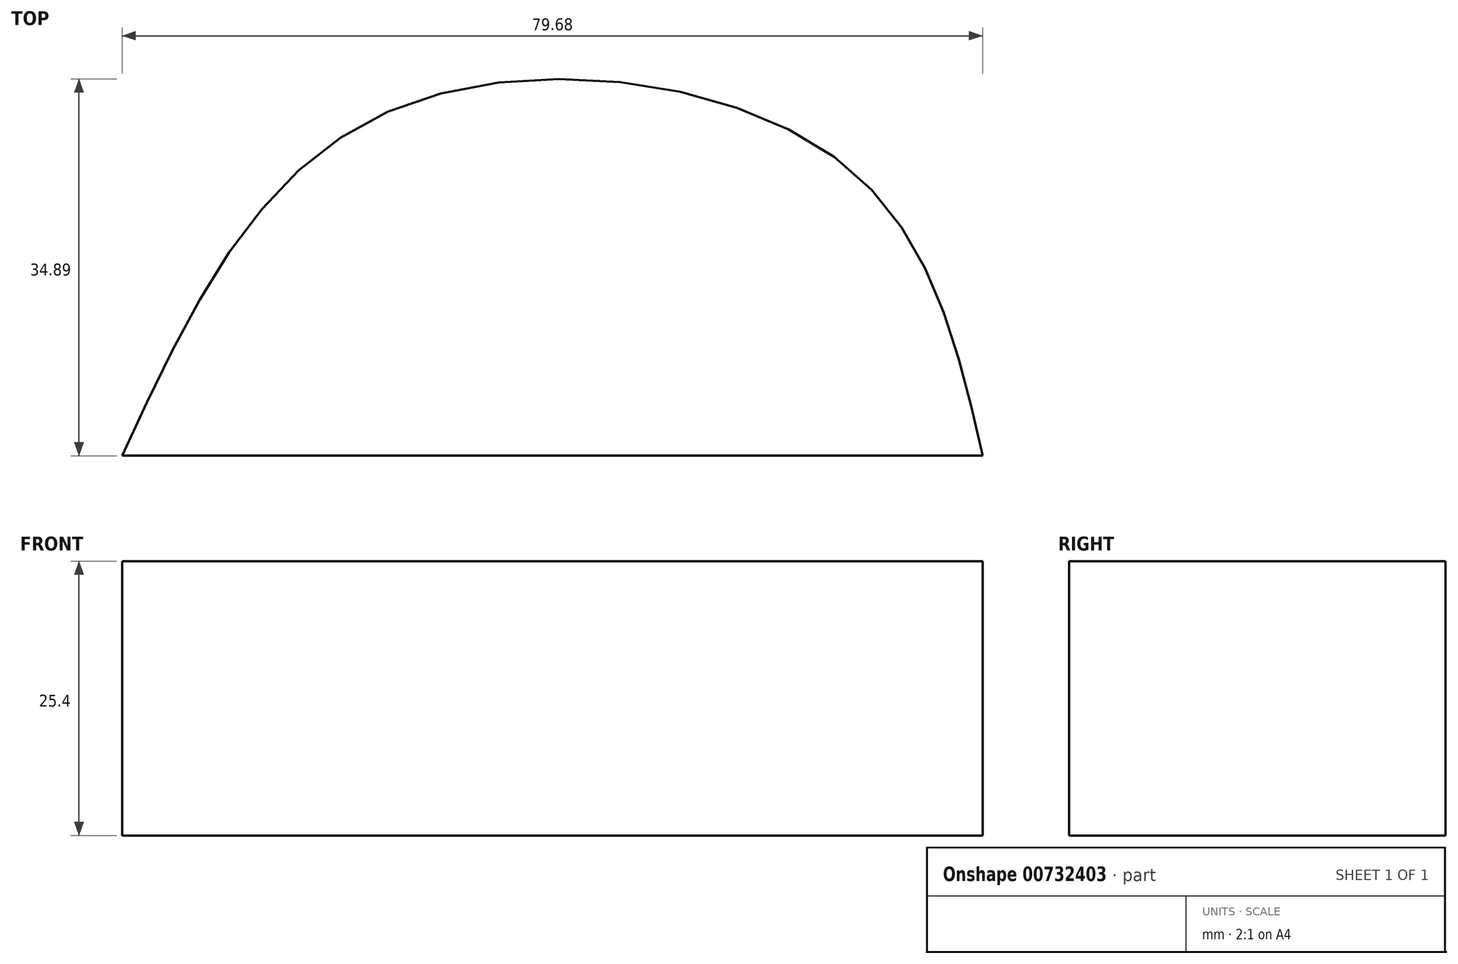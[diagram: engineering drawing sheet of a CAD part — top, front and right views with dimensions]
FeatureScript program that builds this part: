
annotation { "Feature Type Name" : "Feature", "Feature Type Description" : "" }
export const myFeature = defineFeature(function(context is Context, id is Id, definition is map)
    precondition{}
    {
        {
            var Q0;
            Q0=qCreatedBy(makeId("Top.planeOp"),FACE);
            var sketch = newSketch(context, id + "F0", { "sketchPlane" : qUnion([Q0])});
            skLineSegment(sketch, "E0", {"start": v(-113.46, 49.16) * mm, "end": v(-113.46, -27.26) * mm});
            skLineSegment(sketch, "E1", {"start": v(-113.46, -27.26) * mm, "end": v(100.4, -27.26) * mm});
            skLineSegment(sketch, "E2", {"start": v(100.4, -27.26) * mm, "end": v(100.4, 49.16) * mm});
            skLineSegment(sketch, "E3.top", {"start": v(-113.46, 75.25) * mm, "end": v(-7.22, 75.25) * mm});
            skLineSegment(sketch, "E3.left", {"start": v(-113.46, 49.16) * mm, "end": v(-113.46, 75.25) * mm});
            skLineSegment(sketch, "E3.right", {"start": v(-7.22, 49.16) * mm, "end": v(-7.22, 75.25) * mm});
            skCircle(sketch, "E4", {"center": v(100.4, -27.26) * mm, "radius": 20.7 * mm});
            skArc(sketch, "E5", {"start": v(122.3, 6.3) * mm, "mid": v(119.2, 31.73) * mm, "end": v(100.4, 49.16) * mm});
            skFitSpline(sketch, "E6", {"points": [v(122.3, 6.3) * mm, v(129.76, -16.07) * mm, v(119.74, -34.66) * mm], "startDerivative": vector(23.53, -44.9) * mm, "endDerivative": vector(-29.12, -36.95) * mm});
            skFitSpline(sketch, "E7", {"points": [v(-113.46, -27.26) * mm, v(-89.23, -58.94) * mm, v(-47.3, -54.75) * mm, v(-33.78, -27.26) * mm], "startDerivative": vector(52.37, -113.84) * mm, "endDerivative": vector(23.56, 104.18) * mm});
            skLineSegment(sketch, "E8", {"start": v(-7.22, 49.16) * mm, "end": v(100.4, 49.16) * mm});
            skFitSpline(sketch, "E9.MirrorCS", {"points": [v(-113.46, -27.26) * mm, v(-89.23, 4.43) * mm, v(-47.3, 0.23) * mm, v(-33.78, -27.26) * mm], "startDerivative": vector(52.37, 113.84) * mm, "endDerivative": vector(23.56, -104.18) * mm});
            skSolve(sketch);
        }
        {
            var Q0;
            {var subQ0=sQuery(id+"F0.wireOp",EDGE,"E9.MirrorCS");Q0=makeQuery(id+"F0.imprint","IMPRINT",FACE,{"disambiguationData":[TD([[makeQuery(id+"F0.imprint","IMPRINT",EDGE,{"derivedFrom":subQ0}),-1.0]])]});}
            extrude(context, id + "F1", {"entities" : qUnion([Q0]), "depth" : 25.4 * mm, "offsetDistance" : 25.4 * mm});
        }
    });
